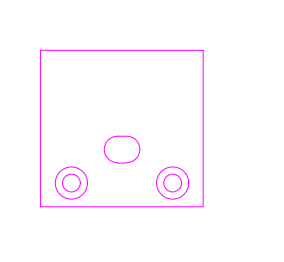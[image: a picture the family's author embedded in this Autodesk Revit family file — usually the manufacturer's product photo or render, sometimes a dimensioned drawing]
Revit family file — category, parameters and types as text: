
# Revit family: S2232 updated
name_source: partatom
category: Lighting Fixtures
units: mm (PartAtom-declared; Revit-internal decimal feet)

## family parameters
Cut with Voids When Loaded = No
Host = Face
Light Source = No
Part Type = Normal
Room Calculation Point = No
Round Connector Dimension = Use Diameter
Shared = Yes

## types (4) — shared parameters
Current Amps = 50 A
Default Elevation = 48 "
Description = Flexible, Linear LED Lighting
Environment = Indoor
Frequency = 60 Hz
Has Battery Backup = No
Has Dimming = Yes
Housing Protection Rating = Consult Manufacturer Website for more Information
Initial Color Comments = Perfomance based on 3000K Photometric Web File
Initial Intensity Comments = Refer LED Strip type for Lumen Value
Input Voltage = 24VDC
LED Tape Documentation link = https://bllighting.com
LED Tape Page URL = https://bllighting.com
LED finish = LED
LED strip = Strip
Lamp Life = 50,000 Hours
Lens Material = Polycarbonate Optic
Load Classification = Lighting
Manufacturer = BL Lighting
Mounting Method = Surface Mount
Number of Poles = 1
Operating Temperature = Consult Manufacturer Website for more Information
Phase = 1
Power Factor = 1
Power Source Type = Driver
Product Documentation Link = https://bllighting.com
Product Page URL = https://bllighting.com
Profile Material = Alumnium Base Track
URL = https://bllighting.com
Version = 2020-v2.9
Voltage = 24 V
Warranty URL = https://bllighting.com

## per-type parameters (varying)
| type | Apparent Load | CCT | Color Option Available | D2 | D3 | D6 | DFD3 | Increment | Lamp | Lumen Output | Max Input Current | Model | Number of LED's | Product Name | Wattage Comments |
| 643 lm per FT 5.85 W per FT - D6 | 120 VA | 2700K,3000K,3500K,4000K | 2700K,3000K,3500K,4000K | No | No | Yes | No | 1.9685 " | LED,SMD 2835 | 643 lm/FT | 5A | D6 | 48 Diodes/FT | D6 | 5.85 W/FT |
| 370 lm per FT 5.5 W per FT - D3 | 120 VA | 2700K,3000K,3500K,4000K,6000K | 2700K,3000K,3500K,4000K,6000K | No | Yes | No | No | 2.4803 " | LED,SMD 5060 | 370 lm/FT | 5A | D3 | 30 Diodes/FT | D3 | 5.5 W/FT |
| 209 lm per FT 3.0W per FT - D2 | 120 VA | 2400K,2700K,3000K,3500K,4000K,5500K,RED,GREEN,BLUE,AMBER | 2400K,2700K,3000K,3500K,4000K,5500K,RED,GREEN,BLUE,AMBER | Yes | No | No | No | 1.9685 " | LED,SMD 3528 | 209 lm/FT | 5 A | D2 | 36 Diodes/FT | D2 | 3.0W/FT |
| 419 lm per FT 4.4 W per FT - DFD3 | 96 VA | 2400K,2700K,3000K,3500K,4000K | 2400K,2700K,3000K,3500K,4000K | No | No | No | Yes | 1.9685 " |  | 419 lm/FT | 4A | DFD3 | 146 Diodes/FT | DFD3 | 4.4W/FT |

## geometry (parser evidence)
native form markers: Sweep x42
no freeform markers — native parametric forms only
